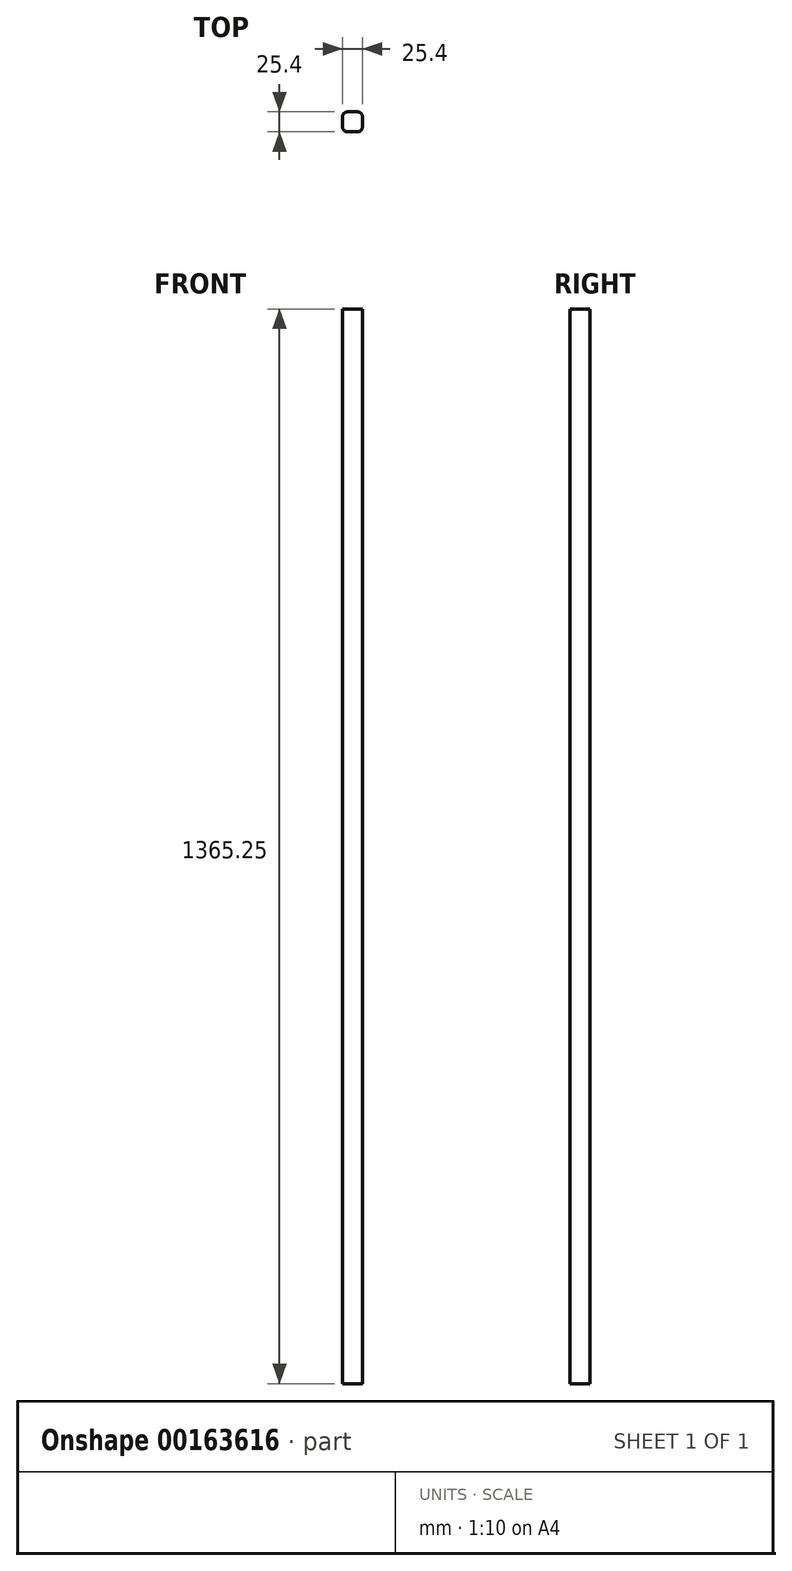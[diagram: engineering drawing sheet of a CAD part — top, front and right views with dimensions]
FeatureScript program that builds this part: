
annotation { "Feature Type Name" : "Feature", "Feature Type Description" : "" }
export const myFeature = defineFeature(function(context is Context, id is Id, definition is map)
    precondition{}
    {
        {
            var Q0;
            Q0=qCreatedBy(makeId("Top.planeOp"),FACE);
            var sketch = newSketch(context, id + "F0", { "sketchPlane" : qUnion([Q0])});
            skLineSegment(sketch, "E0.bottom", {"start": v(6.35, 12.7) * mm, "end": v(-6.35, 12.7) * mm});
            skLineSegment(sketch, "E0.top", {"start": v(6.35, -12.7) * mm, "end": v(-6.35, -12.7) * mm});
            skLineSegment(sketch, "E0.left", {"start": v(12.7, 6.35) * mm, "end": v(12.7, -6.35) * mm});
            skLineSegment(sketch, "E0.right", {"start": v(-12.7, 6.35) * mm, "end": v(-12.7, -6.35) * mm});
            skPoint(sketch, "E0.middle", {"position": v(0, 0) * mm});
            skPoint(sketch, "E1.visualSharp", {"position": v(-12.7, 12.7) * mm});
            skArc(sketch, "E1.filletArc", {"start": v(-6.35, 12.7) * mm, "mid": v(-10.84, 10.84) * mm, "end": v(-12.7, 6.35) * mm});
            skPoint(sketch, "E2.visualSharp", {"position": v(12.7, 12.7) * mm});
            skArc(sketch, "E2.filletArc", {"start": v(12.7, 6.35) * mm, "mid": v(10.84, 10.84) * mm, "end": v(6.35, 12.7) * mm});
            skPoint(sketch, "E3.visualSharp", {"position": v(12.7, -12.7) * mm});
            skArc(sketch, "E3.filletArc", {"start": v(6.35, -12.7) * mm, "mid": v(10.84, -10.84) * mm, "end": v(12.7, -6.35) * mm});
            skPoint(sketch, "E4.visualSharp", {"position": v(-12.7, -12.7) * mm});
            skArc(sketch, "E4.filletArc", {"start": v(-12.7, -6.35) * mm, "mid": v(-10.84, -10.84) * mm, "end": v(-6.35, -12.7) * mm});
            skSolve(sketch);
        }
        {
            var Q0;
            Q0 = qSketchRegion(id + "F0", true);
            extrude(context, id + "F1", {"entities" : qUnion([Q0]), "depth" : 1365.25 * mm});
        }
    });
